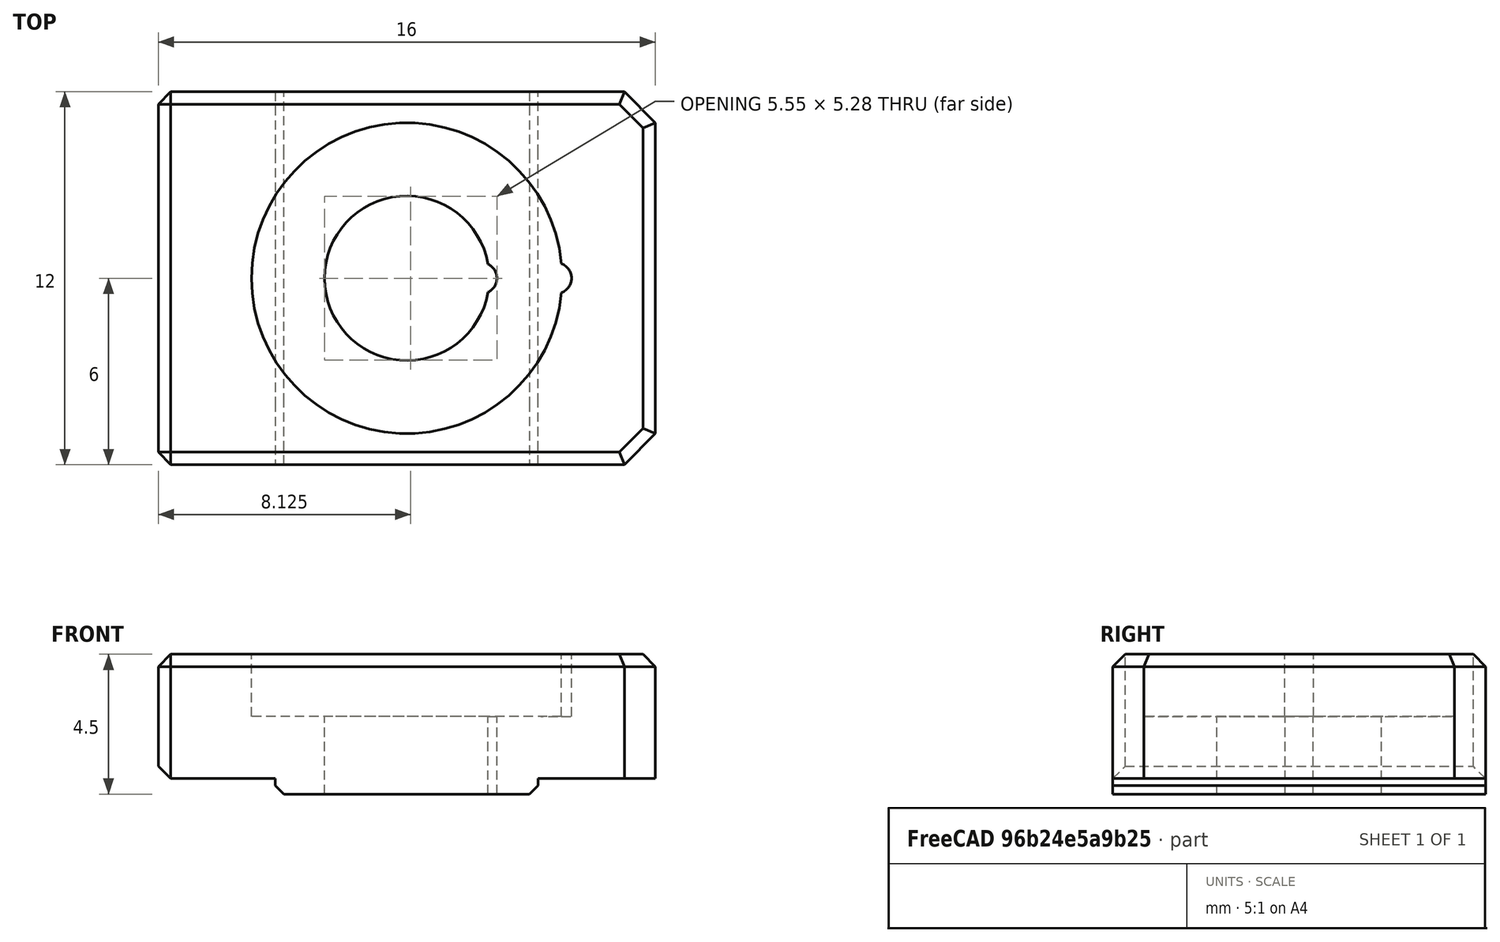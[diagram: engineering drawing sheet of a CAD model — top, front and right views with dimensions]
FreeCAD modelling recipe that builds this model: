
FCSTD DOCUMENT  (FreeCAD 0.18R14555 (Git shallow))
Label: dummy-t-nut-holder
License: All rights reserved
LicenseURL: http://en.wikipedia.org/wiki/All_rights_reserved
objects: Part::Cut×5, Part::Cylinder×4, Part::Feature×2, Part::Box×2, Part::MultiFuse×2, Part::Chamfer×2
note: 17 computed .brp shape members not serialized (recipe doc carries the construction recipe); baked Part::Feature solids carry a one-line shape summary decoded from their .brp

FEATURE [Part::Feature] Part__Feature  label="v-slot-stablizer"
  Placement = pos=(-3.005,-14,0) rot=(0,0,1;0rad)
  shape: bbox 8.45 x 10 x 1.4 mm, 8 faces (baked)
FEATURE [Part::Box] Box  label="Cube"
  AttacherType = Attacher::AttachEngine3D
  Height = 4
  Length = 16
  Width = 12
FEATURE [Part::Feature] Part__Feature001  label="v-slot-stablizer001"
  Placement = pos=(-3.005,-16,0) rot=(0,0,1;0rad)
  shape: bbox 8.45 x 10 x 1.4 mm, 8 faces (baked)
FEATURE [Part::Box] Box001  label="Cube001"
  AttacherType = Attacher::AttachEngine3D
  Height = 3
  Length = 16
  Placement = pos=(0,0,-3.5) rot=(0,0,1;0rad)
  Width = 12
FEATURE [Part::MultiFuse] Fusion
  Shapes = -> [Part__Feature001,Part__Feature]
FEATURE [Part::Cut] Cut
  Base = -> Fusion
  Tool = -> Box001
FEATURE [Part::Cylinder] Cylinder
  Angle = 360
  AttacherType = Attacher::AttachEngine3D
  Height = 10
  Placement = pos=(10.4,6,-5) rot=(0,0,1;0rad)
  Radius = 0.5
FEATURE [Part::Cylinder] Cylinder001
  Angle = 360
  AttacherType = Attacher::AttachEngine3D
  Height = 2
  Placement = pos=(12.8,6,2) rot=(0,0,1;0rad)
  Radius = 0.5
FEATURE [Part::Cylinder] Cylinder002
  Angle = 360
  AttacherType = Attacher::AttachEngine3D
  Height = 2
  Placement = pos=(8,6,2) rot=(0,0,1;0rad)
  Radius = 5
FEATURE [Part::Cylinder] Cylinder003
  Angle = 360
  AttacherType = Attacher::AttachEngine3D
  Height = 10
  Placement = pos=(8,6,-5) rot=(0,0,1;0rad)
  Radius = 2.65
FEATURE [Part::MultiFuse] Fusion001
  Shapes = -> [Box,Cut]
FEATURE [Part::Cut] Cut001
  Base = -> Fusion001
  Tool = -> Cylinder002
FEATURE [Part::Cut] Cut002
  Base = -> Cut001
  Tool = -> Cylinder003
FEATURE [Part::Cut] Cut003
  Base = -> Cut002
  Tool = -> Cylinder001
FEATURE [Part::Cut] Cut004
  Base = -> Cut003
  Tool = -> Cylinder
FEATURE [Part::Chamfer] Chamfer
  Base = -> Cut004
  Edges = 2 edges r=1: [Edge8,Edge18]
FEATURE [Part::Chamfer] Chamfer001
  Base = -> Chamfer
  Edges = 9 edges r=0.4: [Edge4,Edge6,Edge15,Edge21,Edge22,Edge23,Edge24,Edge32,Edge33]
